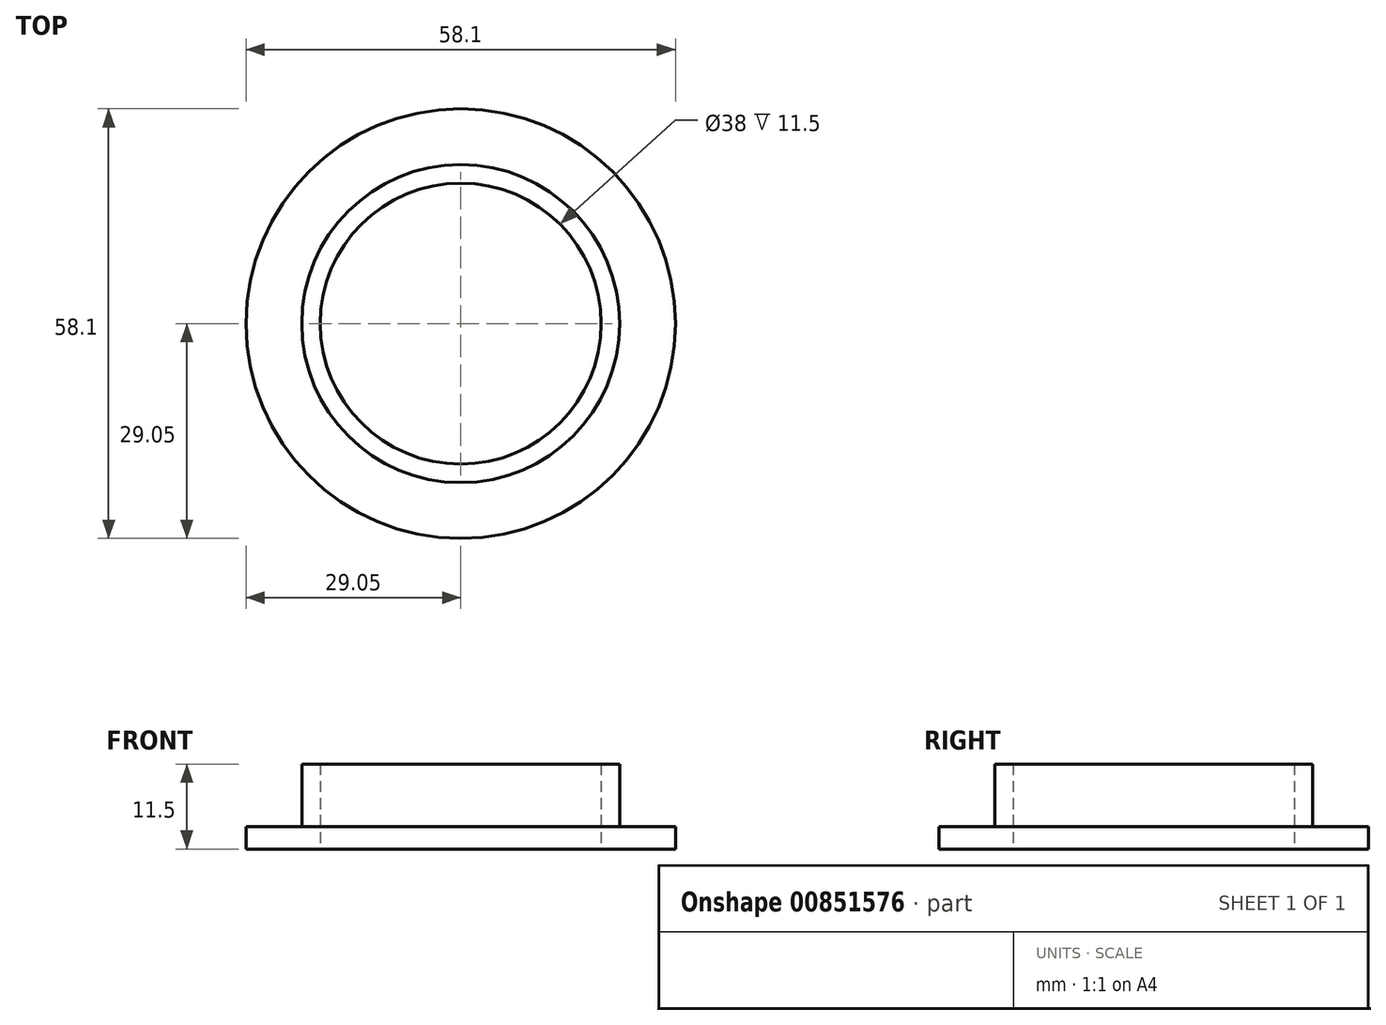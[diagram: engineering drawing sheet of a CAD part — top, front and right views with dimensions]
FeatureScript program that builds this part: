
annotation { "Feature Type Name" : "Feature", "Feature Type Description" : "" }
export const myFeature = defineFeature(function(context is Context, id is Id, definition is map)
    precondition{}
    {
        {
            var Q0;
            Q0=qCreatedBy(makeId("Front.planeOp"),FACE);
            var sketch = newSketch(context, id + "F0", { "sketchPlane" : qUnion([Q0])});
            skLineSegment(sketch, "E0", {"start": v(19, 0) * mm, "end": v(19, 11.5) * mm});
            skLineSegment(sketch, "E1", {"start": v(19, 11.5) * mm, "end": v(21.5, 11.5) * mm});
            skLineSegment(sketch, "E2", {"start": v(21.5, 11.5) * mm, "end": v(21.5, 3) * mm});
            skLineSegment(sketch, "E3", {"start": v(21.5, 3) * mm, "end": v(29.05, 3) * mm});
            skLineSegment(sketch, "E4", {"start": v(29.05, 3) * mm, "end": v(29.05, 0) * mm});
            skLineSegment(sketch, "E5", {"start": v(29.05, 0) * mm, "end": v(19, 0) * mm});
            skLineSegment(sketch, "E6", {"start": v(0, 0) * mm, "end": v(0, 14.53) * mm, "construction": true});
            skSolve(sketch);
        }
        {
            var Q0;
            Q0=qSketchRegion(id+"F0",true);
            var Q1;
            Q1=sQuery(id+"F0.wireOp",EDGE,"E6");
            revolve(context, id + "F1", {"surfaceOperationType" : NewSurfaceOperationType.NEW, "entities" : qUnion([Q0]), "axis" : qUnion([Q1]), "revolveType" : RevolveType.FULL});
        }
    });
